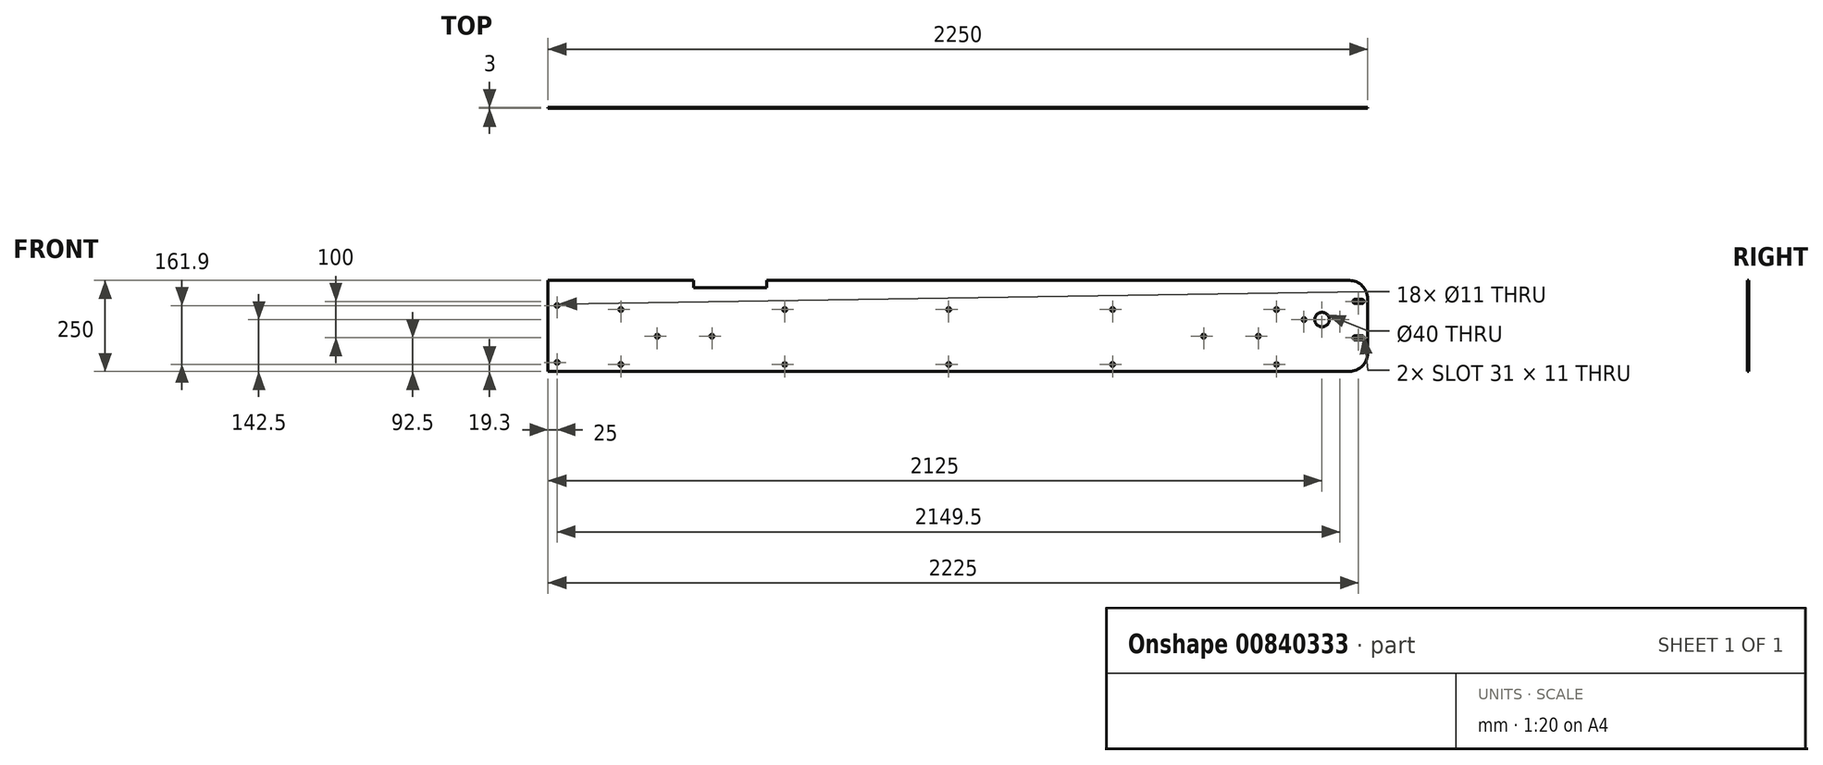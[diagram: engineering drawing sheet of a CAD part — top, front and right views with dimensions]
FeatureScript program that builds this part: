
annotation { "Feature Type Name" : "Feature", "Feature Type Description" : "" }
export const myFeature = defineFeature(function(context is Context, id is Id, definition is map)
    precondition{}
    {
        {
            var Q0;
            Q0=qCreatedBy(makeId("Front.planeOp"),FACE);
            var sketch = newSketch(context, id + "F0", { "sketchPlane" : qUnion([Q0])});
            skLineSegment(sketch, "E0.bottom", {"start": v(-1125, 125) * mm, "end": v(1125, 125) * mm});
            skLineSegment(sketch, "E0.top", {"start": v(-1125, -125) * mm, "end": v(1125, -125) * mm});
            skLineSegment(sketch, "E0.left", {"start": v(-1125, 125) * mm, "end": v(-1125, -125) * mm});
            skLineSegment(sketch, "E0.right", {"start": v(1125, 125) * mm, "end": v(1125, -125) * mm});
            skPoint(sketch, "E0.middle", {"position": v(0, 0) * mm});
            skSolve(sketch);
        }
        {
            var Q0;
            Q0=qSketchRegion(id+"F0",true);
            extrude(context, id + "F1", {"entities" : qUnion([Q0]), "endBound" : BoundingType.SYMMETRIC, "depth" : 3 * mm, "offsetDistance" : 25 * mm});
        }
        {
            var Q0;
            Q0=makeQuery(id+"F1.opExtrude","CAP_FACE",FACE,{"disambiguationData":[OSD([sQuery(id+"F0.wireOp",EDGE,"E0.bottom"),sQuery(id+"F0.wireOp",EDGE,"E0.top"),sQuery(id+"F0.wireOp",EDGE,"E0.left"),sQuery(id+"F0.wireOp",EDGE,"E0.right")])],"isStart":false});
            var sketch = newSketch(context, id + "F2", { "sketchPlane" : qUnion([Q0])});
            skPoint(sketch, "E1", {"position": v(-1100, -100) * mm});
            skPoint(sketch, "E2", {"position": v(-1100, 56.2) * mm});
            skPoint(sketch, "E3", {"position": v(-925, -105.7) * mm});
            skPoint(sketch, "E4", {"position": v(-925, 45.1) * mm});
            skPoint(sketch, "E5", {"position": v(675, -28) * mm});
            skPoint(sketch, "E6", {"position": v(825, -28) * mm});
            skPoint(sketch, "E7", {"position": v(875, 45.1) * mm});
            skPoint(sketch, "E8", {"position": v(875, -105.7) * mm});
            skPoint(sketch, "E9", {"position": v(425, -105.7) * mm});
            skPoint(sketch, "E10", {"position": v(425, 45.1) * mm});
            skPoint(sketch, "E11", {"position": v(-25, 45.1) * mm});
            skPoint(sketch, "E12", {"position": v(-25, -105.7) * mm});
            skPoint(sketch, "E13", {"position": v(-475, 45.1) * mm});
            skPoint(sketch, "E14", {"position": v(-475, -105.7) * mm});
            skPoint(sketch, "E15", {"position": v(-675, -28) * mm});
            skPoint(sketch, "E16", {"position": v(-825, -28) * mm});
            skSolve(sketch);
        }
        {
            var Q0;
            Q0=sQuery(id+"F2.wireOp",VERTEX,"E2");
            var Q1;
            Q1=sQuery(id+"F2.wireOp",VERTEX,"E1");
            var Q2;
            Q2=sQuery(id+"F2.wireOp",VERTEX,"E3");
            var Q3;
            Q3=sQuery(id+"F2.wireOp",VERTEX,"E4");
            var Q4;
            Q4=sQuery(id+"F2.wireOp",VERTEX,"E5");
            var Q5;
            Q5=sQuery(id+"F2.wireOp",VERTEX,"E6");
            var Q6;
            Q6=sQuery(id+"F2.wireOp",VERTEX,"E8");
            var Q7;
            Q7=sQuery(id+"F2.wireOp",VERTEX,"E7");
            var Q8;
            Q8=sQuery(id+"F2.wireOp",VERTEX,"E13");
            var Q9;
            Q9=sQuery(id+"F2.wireOp",VERTEX,"E14");
            var Q10;
            Q10=sQuery(id+"F2.wireOp",VERTEX,"E12");
            var Q11;
            Q11=sQuery(id+"F2.wireOp",VERTEX,"E11");
            var Q12;
            Q12=sQuery(id+"F2.wireOp",VERTEX,"E10");
            var Q13;
            Q13=sQuery(id+"F2.wireOp",VERTEX,"E9");
            var Q14;
            Q14=sQuery(id+"F2.wireOp",VERTEX,"E16");
            var Q15;
            Q15=sQuery(id+"F2.wireOp",VERTEX,"E15");
            var Q16;
            Q16=makeQuery(id+"F1.opExtrude","SWEPT_BODY",BODY,{"disambiguationData":[OSD([sQuery(id+"F0.wireOp",EDGE,"E0.bottom"),sQuery(id+"F0.wireOp",EDGE,"E0.top"),sQuery(id+"F0.wireOp",EDGE,"E0.left"),sQuery(id+"F0.wireOp",EDGE,"E0.right")])]});
            hole(context, id + "F3", {"style" : HoleStyle.SIMPLE, "endStyle" : HoleEndStyle.BLIND, "standardTappedOrClearance" : lookupTablePath({ "fit" : "Normal", "standard" : "ISO", "size" : "M10", "type" : "Clearance" }), "standardBlindInLast" : lookupTablePath({ "fit" : "Standard", "standard" : "ISO", "size" : "M10", "type" : "Clearance" }), "holeDiameter" : 11 * mm, "majorDiameter" : 16 * mm, "holeDepth" : 18 * mm, "isTappedThrough" : true, "tappedDepth" : 12 * mm, "tapClearance" : 3, "startFromSketch" : true, "locations" : qUnion([Q0, Q1, Q2, Q3, Q4, Q5, Q6, Q7, Q8, Q9, Q10, Q11, Q12, Q13, Q14, Q15]), "scope" : qUnion([Q16])});
        }
        {
            var Q0;
            Q0=makeQuery(id+"F1.opExtrude","CAP_FACE",FACE,{"disambiguationData":[OSD([sQuery(id+"F0.wireOp",EDGE,"E0.bottom"),sQuery(id+"F0.wireOp",EDGE,"E0.top"),sQuery(id+"F0.wireOp",EDGE,"E0.left"),sQuery(id+"F0.wireOp",EDGE,"E0.right")])],"isStart":false});
            var sketch = newSketch(context, id + "F4", { "sketchPlane" : qUnion([Q0])});
            skLineSegment(sketch, "E17", {"start": v(1110, -32.5) * mm, "end": v(1090, -32.5) * mm});
            skLineSegment(sketch, "E18", {"start": v(1110, 67.5) * mm, "end": v(1090, 67.5) * mm});
            skArc(sketch, "E19.0.startCap", {"start": v(1110, 73) * mm, "mid": v(1115.5, 67.5) * mm, "end": v(1110, 62) * mm});
            skArc(sketch, "E19.0.endCap", {"start": v(1090, 62) * mm, "mid": v(1084.5, 67.5) * mm, "end": v(1090, 73) * mm});
            skLineSegment(sketch, "E19.0.left", {"start": v(1110, 62) * mm, "end": v(1090, 62) * mm});
            skLineSegment(sketch, "E19.0.right", {"start": v(1110, 73) * mm, "end": v(1090, 73) * mm});
            skArc(sketch, "E19.1.startCap", {"start": v(1110, -27) * mm, "mid": v(1115.5, -32.5) * mm, "end": v(1110, -38) * mm});
            skArc(sketch, "E19.1.endCap", {"start": v(1090, -38) * mm, "mid": v(1084.5, -32.5) * mm, "end": v(1090, -27) * mm});
            skLineSegment(sketch, "E19.1.left", {"start": v(1110, -38) * mm, "end": v(1090, -38) * mm});
            skLineSegment(sketch, "E19.1.right", {"start": v(1110, -27) * mm, "end": v(1090, -27) * mm});
            skSolve(sketch);
        }
        {
            var Q0;
            Q0=qSketchRegion(id+"F4",true);
            extrude(context, id + "F5", {"entities" : qUnion([Q0]), "operationType" : NewBodyOperationType.REMOVE, "endBound" : BoundingType.THROUGH_ALL, "oppositeDirection" : true, "depth" : 25 * mm, "offsetDistance" : 25 * mm});
        }
        {
            var Q0;
            Q0=makeQuery(id+"F1.opExtrude","CAP_FACE",FACE,{"disambiguationData":[OSD([sQuery(id+"F0.wireOp",EDGE,"E0.bottom"),sQuery(id+"F0.wireOp",EDGE,"E0.top"),sQuery(id+"F0.wireOp",EDGE,"E0.left"),sQuery(id+"F0.wireOp",EDGE,"E0.right")])],"isStart":false});
            var sketch = newSketch(context, id + "F6", { "sketchPlane" : qUnion([Q0])});
            skCircle(sketch, "E20", {"center": v(1000, 17.5) * mm, "radius": 20 * mm});
            skSolve(sketch);
        }
        {
            var Q0;
            Q0=qSketchRegion(id+"F6",true);
            extrude(context, id + "F7", {"entities" : qUnion([Q0]), "operationType" : NewBodyOperationType.REMOVE, "endBound" : BoundingType.THROUGH_ALL, "oppositeDirection" : true, "depth" : 25 * mm, "offsetDistance" : 25 * mm});
        }
        {
            var Q0;
            Q0=makeQuery(id+"F1.opExtrude","CAP_FACE",FACE,{"disambiguationData":[OSD([sQuery(id+"F0.wireOp",EDGE,"E0.bottom"),sQuery(id+"F0.wireOp",EDGE,"E0.top"),sQuery(id+"F0.wireOp",EDGE,"E0.left"),sQuery(id+"F0.wireOp",EDGE,"E0.right")])],"isStart":false});
            var sketch = newSketch(context, id + "F8", { "sketchPlane" : qUnion([Q0])});
            skPoint(sketch, "E21", {"position": v(950.5, 17.5) * mm});
            skPoint(sketch, "E22", {"position": v(1049.5, 17.5) * mm});
            skLineSegment(sketch, "E23", {"start": v(1049.5, 17.5) * mm, "end": v(950.5, 17.5) * mm, "construction": true});
            skPoint(sketch, "E24", {"position": v(1000, 17.5) * mm});
            skSolve(sketch);
        }
        {
            var Q0;
            Q0=sQuery(id+"F8.wireOp",VERTEX,"E21");
            var Q1;
            Q1=sQuery(id+"F8.wireOp",VERTEX,"E22");
            var Q2;
            Q2=makeQuery(id+"F1.opExtrude","SWEPT_BODY",BODY,{"disambiguationData":[OSD([sQuery(id+"F0.wireOp",EDGE,"E0.bottom"),sQuery(id+"F0.wireOp",EDGE,"E0.top"),sQuery(id+"F0.wireOp",EDGE,"E0.left"),sQuery(id+"F0.wireOp",EDGE,"E0.right")])]});
            hole(context, id + "F9", {"style" : HoleStyle.SIMPLE, "endStyle" : HoleEndStyle.BLIND, "standardTappedOrClearance" : lookupTablePath({ "fit" : "Normal", "standard" : "ISO", "size" : "M10", "type" : "Clearance" }), "standardBlindInLast" : lookupTablePath({ "fit" : "Standard", "standard" : "ISO", "size" : "M10", "type" : "Clearance" }), "holeDiameter" : 11 * mm, "majorDiameter" : 5 * mm, "holeDepth" : 18 * mm, "isTappedThrough" : true, "tappedDepth" : 12 * mm, "tapClearance" : 3, "startFromSketch" : true, "locations" : qUnion([Q0, Q1]), "scope" : qUnion([Q2])});
        }
        {
            var Q0;
            Q0=makeQuery(id+"F1.opExtrude","SWEPT_EDGE",EDGE,{"disambiguationData":[OSD([sQuery(id+"F0.wireOp",EDGE,"E0.bottom"),sQuery(id+"F0.wireOp",EDGE,"E0.right")])]});
            var Q1;
            Q1=makeQuery(id+"F1.opExtrude","SWEPT_EDGE",EDGE,{"disambiguationData":[OSD([sQuery(id+"F0.wireOp",EDGE,"E0.top"),sQuery(id+"F0.wireOp",EDGE,"E0.right")])]});
            fillet(context, id + "F10", {"entities" : qUnion([Q0, Q1]), "radius" : 50 * mm, "tangentPropagation" : true, "allowEdgeOverflow" : false});
        }
        {
            var Q0;
            Q0=makeQuery(id+"F1.opExtrude","CAP_FACE",FACE,{"disambiguationData":[OSD([sQuery(id+"F0.wireOp",EDGE,"E0.bottom"),sQuery(id+"F0.wireOp",EDGE,"E0.top"),sQuery(id+"F0.wireOp",EDGE,"E0.left"),sQuery(id+"F0.wireOp",EDGE,"E0.right")])],"isStart":false});
            var sketch = newSketch(context, id + "F11", { "sketchPlane" : qUnion([Q0])});
            skLineSegment(sketch, "E25.bottom", {"start": v(-725, 125) * mm, "end": v(-525, 125) * mm});
            skLineSegment(sketch, "E25.top", {"start": v(-725, 105) * mm, "end": v(-525, 105) * mm});
            skLineSegment(sketch, "E25.left", {"start": v(-725, 125) * mm, "end": v(-725, 105) * mm});
            skLineSegment(sketch, "E25.right", {"start": v(-525, 125) * mm, "end": v(-525, 105) * mm});
            skSolve(sketch);
        }
        {
            var Q0;
            Q0=makeQuery(id+"F11.imprint","IMPRINT",FACE,{"disambiguationData":[TD([[makeQuery(id+"F11.imprint","IMPRINT",EDGE,{"derivedFrom":sQuery(id+"F11.wireOp",EDGE,"E25.bottom")}),-1.0]])]});
            extrude(context, id + "F12", {"entities" : qUnion([Q0]), "operationType" : NewBodyOperationType.REMOVE, "endBound" : BoundingType.THROUGH_ALL, "oppositeDirection" : true, "depth" : 25 * mm, "offsetDistance" : 25 * mm});
        }
    });
